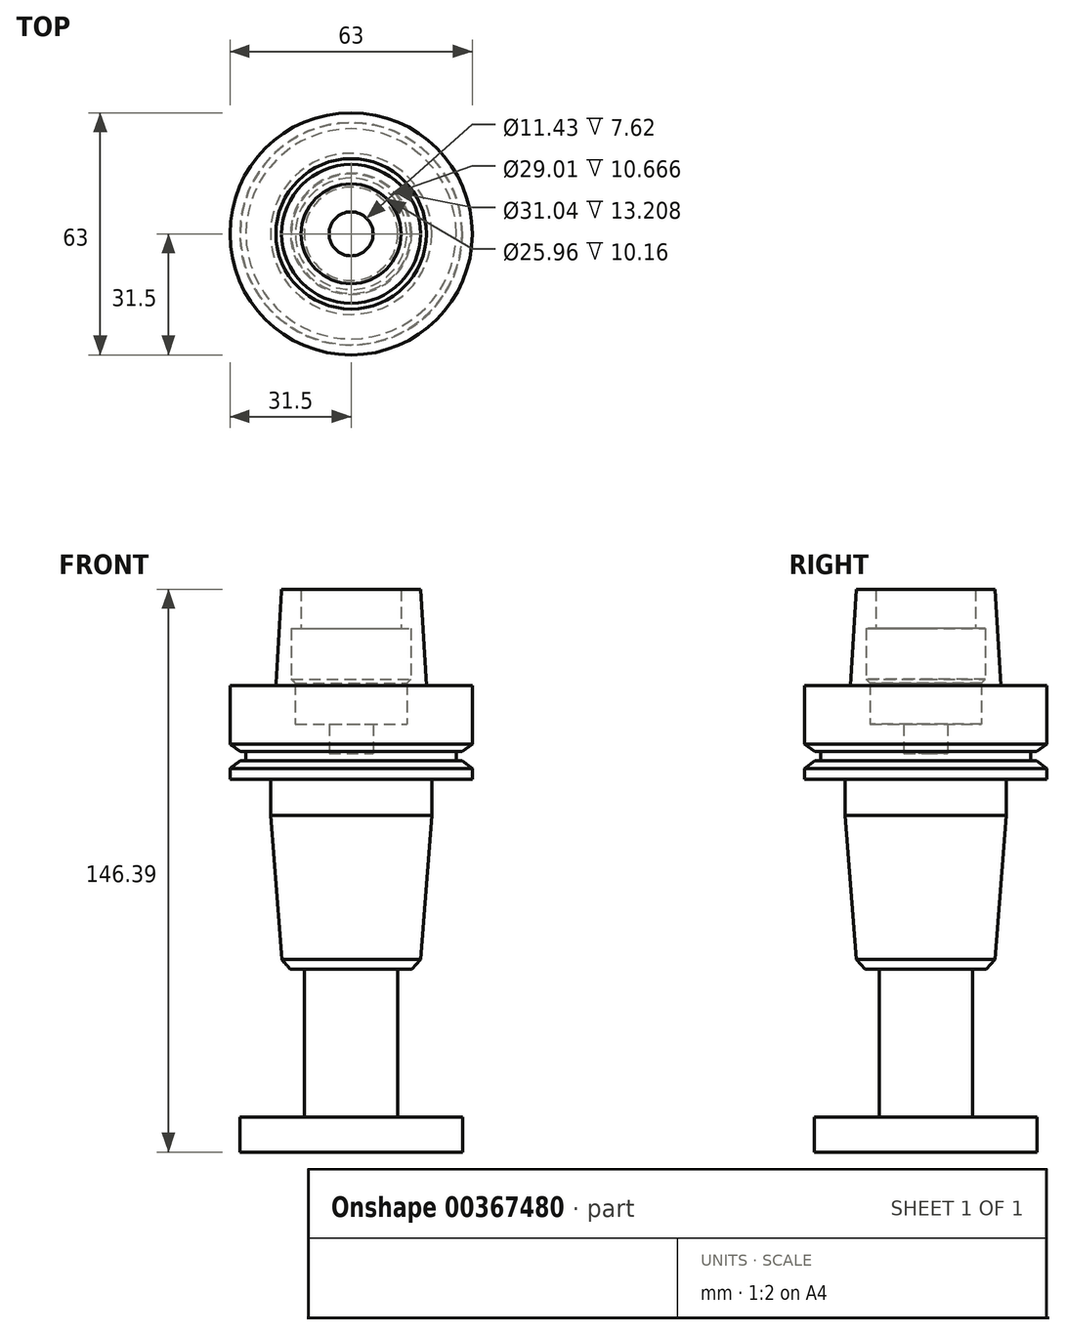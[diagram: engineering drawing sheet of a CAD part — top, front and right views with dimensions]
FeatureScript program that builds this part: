
annotation { "Feature Type Name" : "Feature", "Feature Type Description" : "" }
export const myFeature = defineFeature(function(context is Context, id is Id, definition is map)
    precondition{}
    {
        {
            var Q0;
            Q0=qCreatedBy(makeId("Front.planeOp"),FACE);
            var sketch = newSketch(context, id + "F0", { "sketchPlane" : qUnion([Q0])});
            skLineSegment(sketch, "E0", {"start": v(0, 0) * mm, "end": v(0, 231.66) * mm, "construction": true});
            skLineSegment(sketch, "E1", {"start": v(-12.98, 200.04) * mm, "end": v(-18.06, 200.04) * mm});
            skLineSegment(sketch, "E2", {"start": v(-18.06, 200.04) * mm, "end": v(-19.56, 175.02) * mm});
            skLineSegment(sketch, "E3", {"start": v(-19.56, 175.02) * mm, "end": v(-31.5, 175.02) * mm});
            skLineSegment(sketch, "E4", {"start": v(-31.5, 175.02) * mm, "end": v(-31.5, 159.78) * mm});
            skLineSegment(sketch, "E5", {"start": v(-31.5, 159.78) * mm, "end": v(-28.83, 157.88) * mm});
            skLineSegment(sketch, "E6", {"start": v(-28.83, 157.88) * mm, "end": v(-27.33, 157.88) * mm});
            skLineSegment(sketch, "E7", {"start": v(-27.33, 157.88) * mm, "end": v(-27.33, 155.45) * mm});
            skLineSegment(sketch, "E8", {"start": v(-27.33, 155.45) * mm, "end": v(-28.83, 155.45) * mm});
            skLineSegment(sketch, "E9", {"start": v(-28.83, 155.45) * mm, "end": v(-31.5, 153.43) * mm});
            skLineSegment(sketch, "E10", {"start": v(-31.5, 153.43) * mm, "end": v(-31.5, 150.57) * mm});
            skLineSegment(sketch, "E11", {"start": v(-31.5, 150.57) * mm, "end": v(-20.96, 150.57) * mm});
            skLineSegment(sketch, "E12", {"start": v(-18.03, 103.72) * mm, "end": v(-15.77, 101.18) * mm});
            skLineSegment(sketch, "E13", {"start": v(-15.77, 101.18) * mm, "end": v(-12.14, 101.18) * mm});
            skLineSegment(sketch, "E14", {"start": v(-12.14, 101.18) * mm, "end": v(-12.14, 62.7) * mm});
            skLineSegment(sketch, "E15", {"start": v(-12.14, 62.7) * mm, "end": v(-28.96, 62.7) * mm});
            skLineSegment(sketch, "E16", {"start": v(-28.96, 62.7) * mm, "end": v(-28.96, 53.65) * mm});
            skLineSegment(sketch, "E17", {"start": v(-28.96, 53.65) * mm, "end": v(0, 53.65) * mm});
            skLineSegment(sketch, "E18", {"start": v(0, 53.65) * mm, "end": v(-28.96, 53.65) * mm});
            skPoint(sketch, "E18.endSnap0", {"position": v(-14.48, 53.65) * mm});
            skLineSegment(sketch, "E19", {"start": v(-20.96, 150.57) * mm, "end": v(-20.95, 141.23) * mm});
            skLineSegment(sketch, "E20", {"start": v(-20.95, 141.23) * mm, "end": v(-18.03, 103.72) * mm});
            skLineSegment(sketch, "E21", {"start": v(-12.98, 200.04) * mm, "end": v(-12.98, 189.88) * mm});
            skLineSegment(sketch, "E22", {"start": v(-12.98, 189.88) * mm, "end": v(-15.52, 189.88) * mm});
            skLineSegment(sketch, "E23", {"start": v(-15.52, 189.88) * mm, "end": v(-15.52, 176.67) * mm});
            skLineSegment(sketch, "E24", {"start": v(-15.52, 176.67) * mm, "end": v(-14.5, 175.65) * mm});
            skLineSegment(sketch, "E25", {"start": v(-14.5, 175.65) * mm, "end": v(-14.5, 164.99) * mm});
            skLineSegment(sketch, "E26", {"start": v(-14.5, 164.99) * mm, "end": v(-5.72, 164.99) * mm});
            skLineSegment(sketch, "E27", {"start": v(-5.72, 164.99) * mm, "end": v(-5.71, 157.37) * mm});
            skLineSegment(sketch, "E28", {"start": v(-5.71, 157.37) * mm, "end": v(0, 157.37) * mm});
            skLineSegment(sketch, "E29", {"start": v(0, 157.37) * mm, "end": v(0, 50.5) * mm});
            skPoint(sketch, "E30.start.orphan", {"position": v(-109.37, 53.65) * mm});
            skSolve(sketch);
        }
        {
            var Q0;
            Q0=makeQuery(id+"F0.imprint","IMPRINT",FACE,{"disambiguationData":[TD([[makeQuery(id+"F0.imprint","IMPRINT",EDGE,{"derivedFrom":sQuery(id+"F0.wireOp",EDGE,"E1")}),1.0]])]});
            var Q1;
            Q1=sQuery(id+"F0.wireOp",EDGE,"E0");
            revolve(context, id + "F1", {"entities" : qUnion([Q0]), "axis" : qUnion([Q1]), "revolveType" : RevolveType.FULL});
        }
    });
